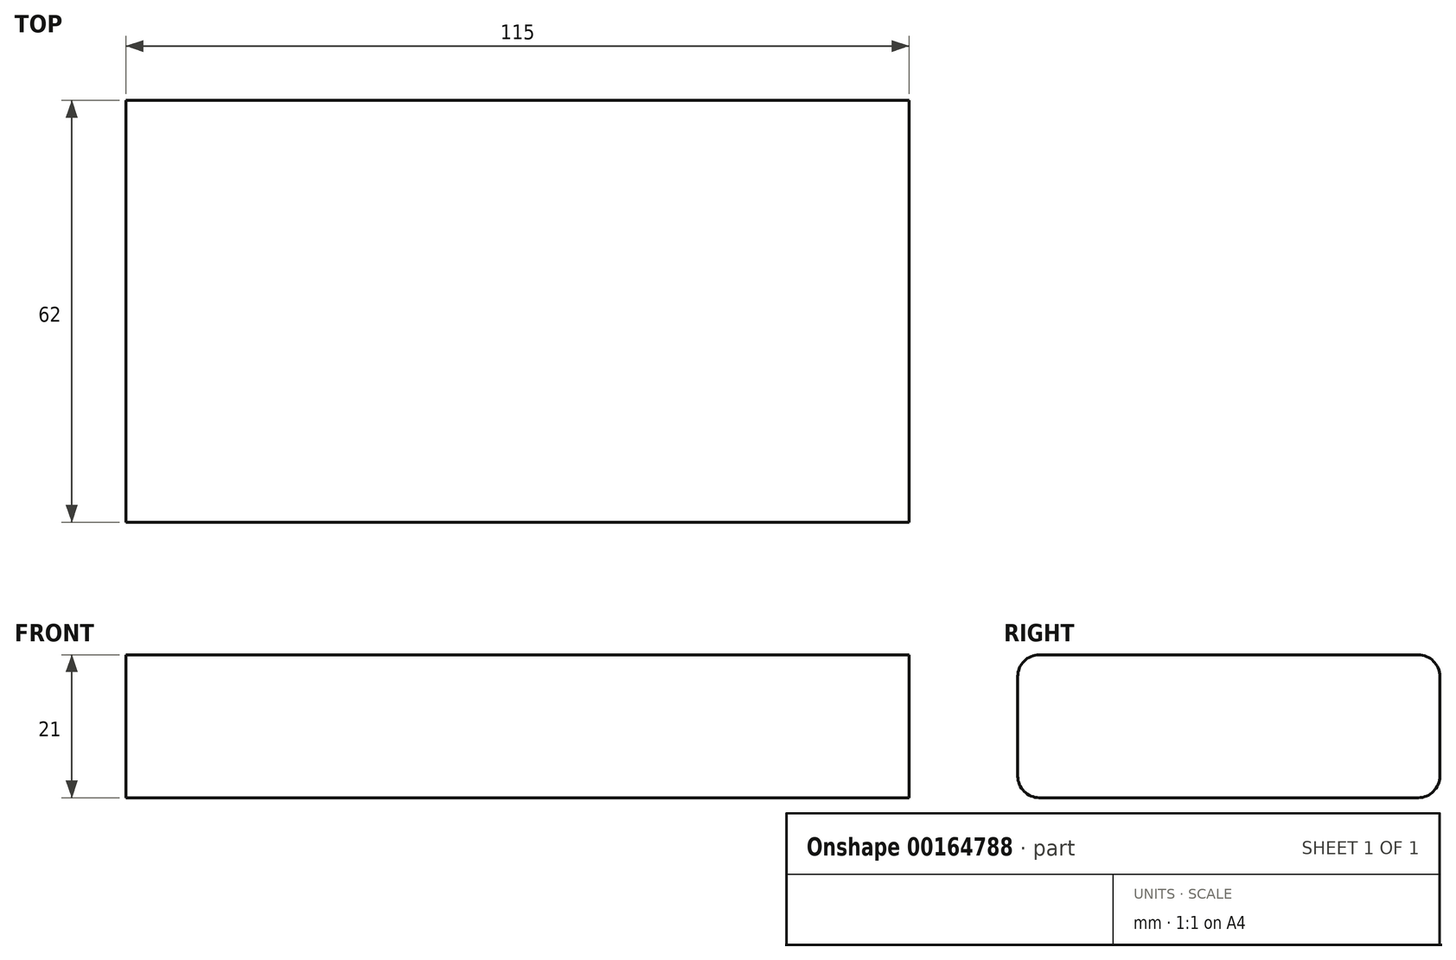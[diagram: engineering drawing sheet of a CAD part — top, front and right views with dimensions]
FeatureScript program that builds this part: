
annotation { "Feature Type Name" : "Feature", "Feature Type Description" : "" }
export const myFeature = defineFeature(function(context is Context, id is Id, definition is map)
    precondition{}
    {
        {
            var Q0;
            Q0=qCreatedBy(makeId("Top.planeOp"),FACE);
            var sketch = newSketch(context, id + "F0", { "sketchPlane" : qUnion([Q0])});
            skLineSegment(sketch, "E0.bottom", {"start": v(0, 0) * mm, "end": v(115, 0) * mm});
            skLineSegment(sketch, "E0.top", {"start": v(0, -62) * mm, "end": v(115, -62) * mm});
            skLineSegment(sketch, "E0.left", {"start": v(0, 0) * mm, "end": v(0, -62) * mm});
            skLineSegment(sketch, "E0.right", {"start": v(115, 0) * mm, "end": v(115, -62) * mm});
            skSolve(sketch);
        }
        {
            var Q0;
            Q0 = qSketchRegion(id + "F0", true);
            extrude(context, id + "F1", {"entities" : qUnion([Q0]), "depth" : 21 * mm});
        }
        {
            var Q0;
            Q0=makeQuery(id+"F1.opExtrude","CAP_EDGE",EDGE,{"disambiguationData":[OSD([sQuery(id+"F0.wireOp",EDGE,"E0.top")])],"isStart":false});
            var Q1;
            Q1=makeQuery(id+"F1.opExtrude","CAP_EDGE",EDGE,{"disambiguationData":[OSD([sQuery(id+"F0.wireOp",EDGE,"E0.bottom")])],"isStart":false});
            var Q2;
            Q2=makeQuery(id+"F1.opExtrude","CAP_EDGE",EDGE,{"disambiguationData":[OSD([sQuery(id+"F0.wireOp",EDGE,"E0.bottom")])],"isStart":true});
            var Q3;
            Q3=makeQuery(id+"F1.opExtrude","CAP_EDGE",EDGE,{"disambiguationData":[OSD([sQuery(id+"F0.wireOp",EDGE,"E0.top")])],"isStart":true});
            fillet(context, id + "F2", {"entities" : qUnion([Q0, Q1, Q2, Q3]), "radius" : 3.17 * mm, "tangentPropagation" : true, "allowEdgeOverflow" : false});
        }
    });
